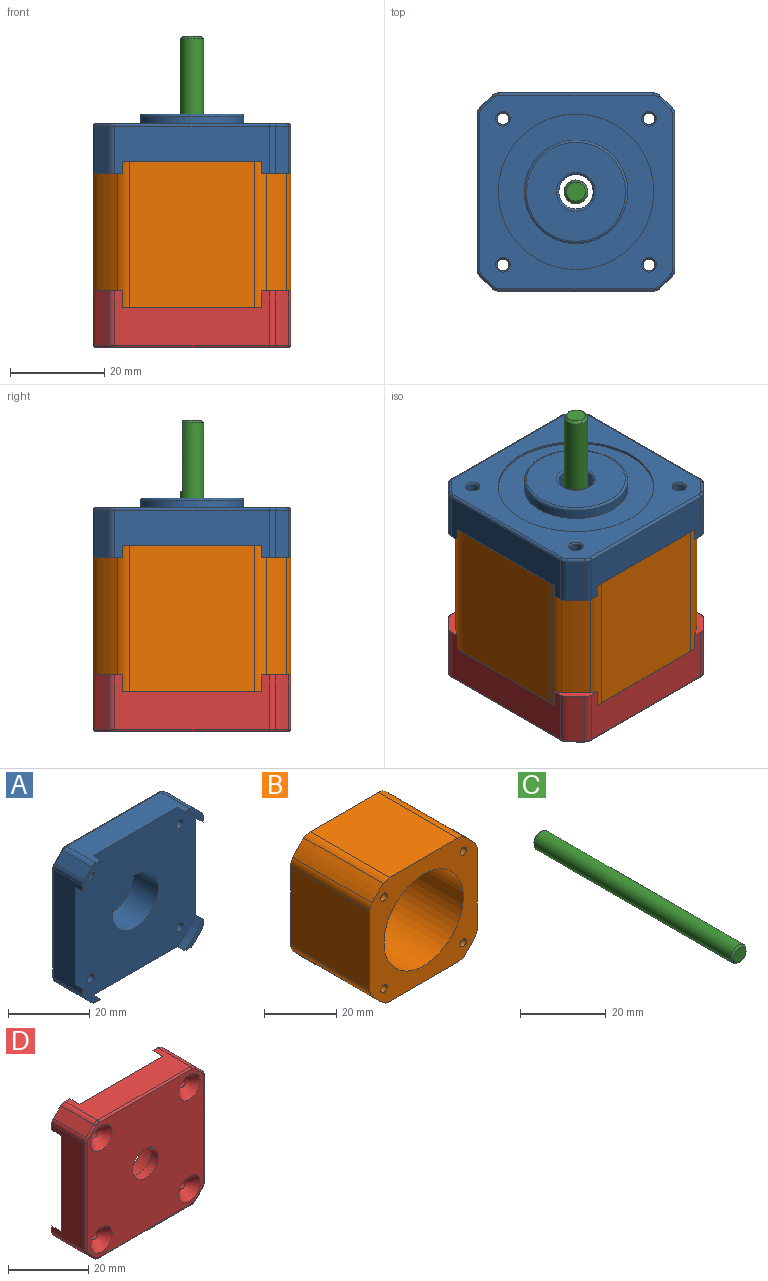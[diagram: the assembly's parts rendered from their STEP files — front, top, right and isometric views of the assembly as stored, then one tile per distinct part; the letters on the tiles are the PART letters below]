
ASSEMBLY  parts=4 mates=3
PART A: 59 faces, bbox 42.3x12.6x42.3 mm
  f0: cylinder r=3.65mm len=7.3mm, axis (0,-1,0), area 20.6mm2, adj f28,f53
  f1: plane 42x42mm, normal (0,-1,0), area 1472mm2, adj f2,f4,f6,f8,f9,f10,f11,f14
  f2: plane 32.74x10.1mm, normal (0,0,1), area 254.6mm2, adj f1,f19,f20,f21,f22,f30,f31,f51
  f3: plane 10.1x2.63mm, normal (0.71,0,0.71), area 37.5mm2, adj f22,f29,f30,f47
  f4: plane 32.74x10.1mm, normal (1,0,0), area 254.6mm2, adj f1,f21,f22,f25,f26,f29,f36,f43
  f5: plane 10.1x2.63mm, normal (0.71,0,-0.71), area 37.5mm2, adj f26,f35,f36,f39
  f6: plane 32.74x10.1mm, normal (0,0,-1), area 254.6mm2, adj f1,f23,f24,f25,f26,f34,f35,f38
  f7: plane 10.1x2.63mm, normal (-0.71,0,-0.71), area 37.5mm2, adj f24,f33,f34,f42
  f8: plane 32.74x10.1mm, normal (-1,0,0), area 254.6mm2, adj f1,f19,f20,f23,f24,f32,f33,f46
  f9: cylinder r=1.25mm len=7.7mm, axis (0,-1,0), area 60.5mm2, adj f1,f58
  f10: cylinder r=1.25mm len=7.7mm, axis (0,-1,0), area 60.5mm2, adj f1,f57
  f11: cylinder r=1.25mm len=7.7mm, axis (0,-1,0), area 60.5mm2, adj f1,f56
  f12: plane 10.1x2.63mm, normal (-0.71,0,0.71), area 37.5mm2, adj f20,f31,f32,f50
  f13: cylinder r=16.5mm len=33mm, axis (0,-1,0), area 51.8mm2, adj f15,f16
  f14: cylinder r=1.25mm len=7.7mm, axis (0,-1,0), area 60.5mm2, adj f1,f55
  f15: plane 41x41mm, normal (0,1,0), area 770.5mm2, adj f13,f37,f38,f39,f40,f41,f42,f43
  f16: plane 33x33mm, normal (0,1,0), area 475.2mm2, adj f13,f17
  f17: cylinder r=11mm len=22mm, axis (0,-1,0), area 138.2mm2, adj f16,f54
  f18: plane 21x21mm, normal (0,1,0), area 292.3mm2, adj f53,f54
  f19: cylinder r=25.6mm len=6.36mm, axis (0,1,0), area 23.5mm2, adj f1,f2,f8,f20
  f20: plane 6.36x6.36mm, normal (0,-1,0), area 10.4mm2, adj f2,f8,f12,f19,f31,f32
  f21: cylinder r=25.6mm len=6.36mm, axis (0,1,0), area 23.5mm2, adj f1,f2,f4,f22
  f22: plane 6.36x6.36mm, normal (0,-1,0), area 10.4mm2, adj f2,f3,f4,f21,f29,f30
  f23: cylinder r=25.6mm len=6.36mm, axis (0,1,0), area 23.5mm2, adj f1,f6,f8,f24
  f24: plane 6.36x6.36mm, normal (0,-1,0), area 10.4mm2, adj f6,f7,f8,f23,f33,f34
  f25: cylinder r=25.6mm len=6.36mm, axis (0,1,0), area 23.5mm2, adj f1,f4,f6,f26
  f26: plane 6.36x6.36mm, normal (0,-1,0), area 10.4mm2, adj f4,f5,f6,f25,f35,f36
  f27: cylinder r=8mm len=16mm, axis (0,-1,0), area 432.3mm2, adj f1,f28
  f28: plane 16x16mm, normal (0,-1,0), area 159.2mm2, adj f0,f27
  f29: cylinder r=2mm len=10.1mm, axis (0,-1,0), area 15.9mm2, adj f3,f4,f22,f45
  f30: cylinder r=2mm len=10.1mm, axis (0,-1,0), area 15.9mm2, adj f2,f3,f22,f49
  f31: cylinder r=2mm len=10.1mm, axis (0,-1,0), area 15.9mm2, adj f2,f12,f20,f52
  f32: cylinder r=2mm len=10.1mm, axis (0,1,0), area 15.9mm2, adj f8,f12,f20,f48
  f33: cylinder r=2mm len=10.1mm, axis (0,-1,0), area 15.9mm2, adj f7,f8,f24,f44
  f34: cylinder r=2mm len=10.1mm, axis (0,-1,0), area 15.9mm2, adj f6,f7,f24,f40
  f35: cylinder r=2mm len=10.1mm, axis (0,-1,0), area 15.9mm2, adj f5,f6,f26,f37
  f36: cylinder r=2mm len=10.1mm, axis (0,1,0), area 15.9mm2, adj f4,f5,f26,f41
  f37: torus R=1.5mm, axis (0,1,0), area 1.1mm2, adj f15,f35,f38,f39
  f38: cylinder r=0.5mm len=32.74mm, axis (1,0,0), area 25.7mm2, adj f6,f15,f37,f40
  f39: cylinder r=0.5mm len=2.98mm, axis (0.71,0,0.71), area 2.9mm2, adj f5,f15,f37,f41
  f40: torus R=1.5mm, axis (0,1,0), area 1.1mm2, adj f15,f34,f38,f42
  f41: torus R=1.5mm, axis (0,1,0), area 1.1mm2, adj f15,f36,f39,f43
  f42: cylinder r=0.5mm len=2.98mm, axis (0.71,0,-0.71), area 2.9mm2, adj f7,f15,f40,f44
  f43: cylinder r=0.5mm len=32.74mm, axis (0,0,1), area 25.7mm2, adj f4,f15,f41,f45
  f44: torus R=1.5mm, axis (0,1,0), area 1.1mm2, adj f15,f33,f42,f46
  f45: torus R=1.5mm, axis (0,1,0), area 1.1mm2, adj f15,f29,f43,f47
  f46: cylinder r=0.5mm len=32.74mm, axis (0,0,-1), area 25.7mm2, adj f8,f15,f44,f48
  f47: cylinder r=0.5mm len=2.98mm, axis (-0.71,0,0.71), area 2.9mm2, adj f3,f15,f45,f49
  f48: torus R=1.5mm, axis (0,1,0), area 1.1mm2, adj f15,f32,f46,f50
  f49: torus R=1.5mm, axis (0,1,0), area 1.1mm2, adj f15,f30,f47,f51
  f50: cylinder r=0.5mm len=2.98mm, axis (-0.71,0,-0.71), area 2.9mm2, adj f12,f15,f48,f52
  f51: cylinder r=0.5mm len=32.74mm, axis (-1,0,0), area 25.7mm2, adj f2,f15,f49,f52
  f52: torus R=1.5mm, axis (0,1,0), area 1.1mm2, adj f15,f31,f50,f51
  f53: torus R=4.15mm, axis (0,1,0), area 18.9mm2, adj f0,f18
  f54: torus R=10.5mm, axis (0,1,0), area 53.4mm2, adj f17,f18
  f55: cone r=1.25mm half-angle=45deg, axis (0,1,0), area 3.7mm2, adj f14,f15
  f56: cone r=1.25mm half-angle=45deg, axis (0,1,0), area 3.7mm2, adj f11,f15
  f57: cone r=1.25mm half-angle=45deg, axis (0,1,0), area 3.7mm2, adj f10,f15
  f58: cone r=1.25mm half-angle=45deg, axis (0,1,0), area 3.7mm2, adj f9,f15
PART B: 23 faces, bbox 42x31x42 mm
  f0: plane 42x42mm, normal (0,1,0), area 916.8mm2, adj f1,f2,f3,f4,f5,f6,f7,f8
  f1: cylinder r=25.6mm len=31mm, axis (0,-1,0), area 191.4mm2, adj f0,f16,f17,f22
  f2: plane 31x26.65mm, normal (0,0,-1), area 826.2mm2, adj f0,f15,f16,f22
  f3: cylinder r=25.6mm len=31mm, axis (0,-1,0), area 191.4mm2, adj f0,f14,f15,f22
  f4: plane 31x26.65mm, normal (-1,0,0), area 826.2mm2, adj f0,f14,f21,f22
  f5: cylinder r=25.6mm len=31mm, axis (0,-1,0), area 191.4mm2, adj f0,f20,f21,f22
  f6: plane 31x26.65mm, normal (0,0,1), area 826.2mm2, adj f0,f19,f20,f22
  f7: cylinder r=25.6mm len=31mm, axis (0,-1,0), area 191.4mm2, adj f0,f18,f19,f22
  f8: plane 31x26.65mm, normal (1,0,0), area 826.2mm2, adj f0,f17,f18,f22
  f9: cylinder r=15.5mm len=31mm, axis (0,-1,0), area 3019.1mm2, adj f0,f22
  f10: cylinder r=1.25mm len=31mm, axis (0,-1,0), area 243.5mm2, adj f0,f22
  f11: cylinder r=1.25mm len=31mm, axis (0,-1,0), area 243.5mm2, adj f0,f22
  f12: cylinder r=1.25mm len=31mm, axis (0,-1,0), area 243.5mm2, adj f0,f22
  f13: cylinder r=1.25mm len=31mm, axis (0,-1,0), area 243.5mm2, adj f0,f22
  f14: cylinder r=4mm len=31mm, axis (0,-1,0), area 82.4mm2, adj f0,f3,f4,f22
  f15: cylinder r=4mm len=31mm, axis (0,-1,0), area 82.4mm2, adj f0,f2,f3,f22
  f16: cylinder r=4mm len=31mm, axis (0,-1,0), area 82.4mm2, adj f0,f1,f2,f22
  f17: cylinder r=4mm len=31mm, axis (0,-1,0), area 82.4mm2, adj f0,f1,f8,f22
  f18: cylinder r=4mm len=31mm, axis (0,-1,0), area 82.4mm2, adj f0,f7,f8,f22
  f19: cylinder r=4mm len=31mm, axis (0,-1,0), area 82.4mm2, adj f0,f6,f7,f22
  f20: cylinder r=4mm len=31mm, axis (0,-1,0), area 82.4mm2, adj f0,f5,f6,f22
  f21: cylinder r=4mm len=31mm, axis (0,-1,0), area 82.4mm2, adj f0,f4,f5,f22
  f22: plane 42x42mm, normal (0,-1,0), area 916.8mm2, adj f1,f2,f3,f4,f5,f6,f7,f8
PART C: 7 faces, bbox 5x66x5 mm
  f0: cylinder r=2.5mm len=65mm, axis (0,-1,0), area 974.4mm2, adj f2,f3,f4,f6
  f1: plane 4x4mm, normal (0,1,0), area 12.6mm2, adj f4
  f2: plane 15x3mm, normal (0,0,-1), area 44.5mm2, adj f0,f3,f4
  f3: plane 3x0.5mm, normal (0,1,0), area 1mm2, adj f0,f2
  f4: cone r=2mm half-angle=45deg, axis (0,-1,0), area 8.6mm2, adj f0,f1,f2
  f5: plane 4x4mm, normal (0,-1,0), area 12.6mm2, adj f6
  f6: cone r=2.5mm half-angle=45deg, axis (0,1,0), area 10mm2, adj f0,f5
PART D: 53 faces, bbox 42.3x12x42.3 mm
  f0: cylinder r=4.5mm len=9mm, axis (0,-1,0), area 70.7mm2, adj f10,f28
  f1: plane 32.74x11.5mm, normal (0,0,1), area 274.1mm2, adj f9,f11,f13,f14,f16,f30,f31,f50
  f2: plane 32.74x11.5mm, normal (1,0,0), area 274.1mm2, adj f9,f11,f13,f20,f22,f29,f36,f42
  f3: plane 32.74x11.5mm, normal (0,0,-1), area 274.1mm2, adj f9,f17,f19,f20,f22,f34,f35,f39
  f4: plane 32.74x11.5mm, normal (-1,0,0), area 274.1mm2, adj f9,f14,f16,f17,f19,f32,f33,f47
  f5: cylinder r=1.25mm len=6mm, axis (0,-1,0), area 47.1mm2, adj f9,f26
  f6: cylinder r=1.25mm len=6mm, axis (0,-1,0), area 47.1mm2, adj f9,f25
  f7: cylinder r=1.25mm len=6mm, axis (0,-1,0), area 47.1mm2, adj f9,f24
  f8: cylinder r=1.25mm len=6mm, axis (0,-1,0), area 47.1mm2, adj f9,f23
  f9: plane 42x42mm, normal (0,1,0), area 1472mm2, adj f1,f2,f3,f4,f5,f6,f7,f8
  f10: plane 41x41mm, normal (0,-1,0), area 1415.7mm2, adj f0,f23,f24,f25,f26,f37,f38,f39
  f11: cylinder r=25.6mm len=6.36mm, axis (0,-1,0), area 31.6mm2, adj f1,f2,f9,f13
  f12: plane 11.5x2.63mm, normal (0.71,0,0.71), area 42.7mm2, adj f13,f29,f30,f46
  f13: plane 6.36x6.36mm, normal (0,1,0), area 10.4mm2, adj f1,f2,f11,f12,f29,f30
  f14: cylinder r=25.6mm len=6.36mm, axis (0,-1,0), area 31.6mm2, adj f1,f4,f9,f16
  f15: plane 11.5x2.63mm, normal (-0.71,0,0.71), area 42.7mm2, adj f16,f31,f32,f51
  f16: plane 6.36x6.36mm, normal (0,1,0), area 10.4mm2, adj f1,f4,f14,f15,f31,f32
  f17: cylinder r=25.6mm len=6.36mm, axis (0,-1,0), area 31.6mm2, adj f3,f4,f9,f19
  f18: plane 11.5x2.63mm, normal (-0.71,0,-0.71), area 42.7mm2, adj f19,f33,f34,f43
  f19: plane 6.36x6.36mm, normal (0,1,0), area 10.4mm2, adj f3,f4,f17,f18,f33,f34
  f20: cylinder r=25.6mm len=6.36mm, axis (0,-1,0), area 31.6mm2, adj f2,f3,f9,f22
  f21: plane 11.5x2.63mm, normal (0.71,0,-0.71), area 42.7mm2, adj f22,f35,f36,f38
  f22: plane 6.36x6.36mm, normal (0,1,0), area 10.4mm2, adj f2,f3,f20,f21,f35,f36
  f23: cone r=3.75mm half-angle=45deg, axis (0,-1,0), area 55.5mm2, adj f8,f10
  f24: cone r=3.75mm half-angle=45deg, axis (0,-1,0), area 55.5mm2, adj f7,f10
  f25: cone r=3.75mm half-angle=45deg, axis (0,-1,0), area 55.5mm2, adj f6,f10
  f26: cone r=3.75mm half-angle=45deg, axis (0,-1,0), area 55.5mm2, adj f5,f10
  f27: cylinder r=8mm len=16mm, axis (0,1,0), area 301.6mm2, adj f9,f28
  f28: plane 16x16mm, normal (0,1,0), area 137.4mm2, adj f0,f27
  f29: cylinder r=2mm len=11.5mm, axis (0,-1,0), area 18.1mm2, adj f2,f12,f13,f44
  f30: cylinder r=2mm len=11.5mm, axis (0,-1,0), area 18.1mm2, adj f1,f12,f13,f48
  f31: cylinder r=2mm len=11.5mm, axis (0,-1,0), area 18.1mm2, adj f1,f15,f16,f52
  f32: cylinder r=2mm len=11.5mm, axis (0,1,0), area 18.1mm2, adj f4,f15,f16,f49
  f33: cylinder r=2mm len=11.5mm, axis (0,-1,0), area 18.1mm2, adj f4,f18,f19,f45
  f34: cylinder r=2mm len=11.5mm, axis (0,-1,0), area 18.1mm2, adj f3,f18,f19,f41
  f35: cylinder r=2mm len=11.5mm, axis (0,-1,0), area 18.1mm2, adj f3,f21,f22,f37
  f36: cylinder r=2mm len=11.5mm, axis (0,1,0), area 18.1mm2, adj f2,f21,f22,f40
  f37: torus R=1.5mm, axis (0,1,0), area 1.1mm2, adj f10,f35,f38,f39
  f38: cylinder r=0.5mm len=2.98mm, axis (-0.71,0,-0.71), area 2.9mm2, adj f10,f21,f37,f40
  f39: cylinder r=0.5mm len=32.74mm, axis (-1,0,0), area 25.7mm2, adj f3,f10,f37,f41
  f40: torus R=1.5mm, axis (0,1,0), area 1.1mm2, adj f10,f36,f38,f42
  f41: torus R=1.5mm, axis (0,1,0), area 1.1mm2, adj f10,f34,f39,f43
  f42: cylinder r=0.5mm len=32.74mm, axis (0,0,-1), area 25.7mm2, adj f2,f10,f40,f44
  f43: cylinder r=0.5mm len=2.98mm, axis (-0.71,0,0.71), area 2.9mm2, adj f10,f18,f41,f45
  f44: torus R=1.5mm, axis (0,1,0), area 1.1mm2, adj f10,f29,f42,f46
  f45: torus R=1.5mm, axis (0,1,0), area 1.1mm2, adj f10,f33,f43,f47
  f46: cylinder r=0.5mm len=2.98mm, axis (0.71,0,-0.71), area 2.9mm2, adj f10,f12,f44,f48
  f47: cylinder r=0.5mm len=32.74mm, axis (0,0,1), area 25.7mm2, adj f4,f10,f45,f49
  f48: torus R=1.5mm, axis (0,1,0), area 1.1mm2, adj f10,f30,f46,f50
  f49: torus R=1.5mm, axis (0,1,0), area 1.1mm2, adj f10,f32,f47,f51
  f50: cylinder r=0.5mm len=32.74mm, axis (1,0,0), area 25.7mm2, adj f1,f10,f48,f52
  f51: cylinder r=0.5mm len=2.98mm, axis (0.71,0,0.71), area 2.9mm2, adj f10,f15,f49,f52
  f52: torus R=1.5mm, axis (0,1,0), area 1.1mm2, adj f10,f31,f50,f51
PLACE A rot(axis=(1,0,0),90deg) t=(-59.47,-14.57,31.4)mm
PLACE B rot(axis=(1,0,0),90deg) t=(-59.47,-14.57,15.4)mm
PLACE C rot(axis=(1,-0.02,-0.02),90deg) t=(-59.47,-14.57,-8.1)mm
PLACE D rot(axis=(1,0,0),90deg) t=(-59.47,-14.57,-8.1)mm fixed
MATE revolute C.f0 <-> D.f0  axis (0,0,1) through (-59.47,-14.57,-8.1)mm
MATE fastened A.f27 <-> B.f1  axis (0,0,-1) through (-59.47,-14.57,31.4)mm
MATE fastened D.f0 <-> B.f1  axis (0,0,1) through (-59.47,-14.57,0.4)mm
